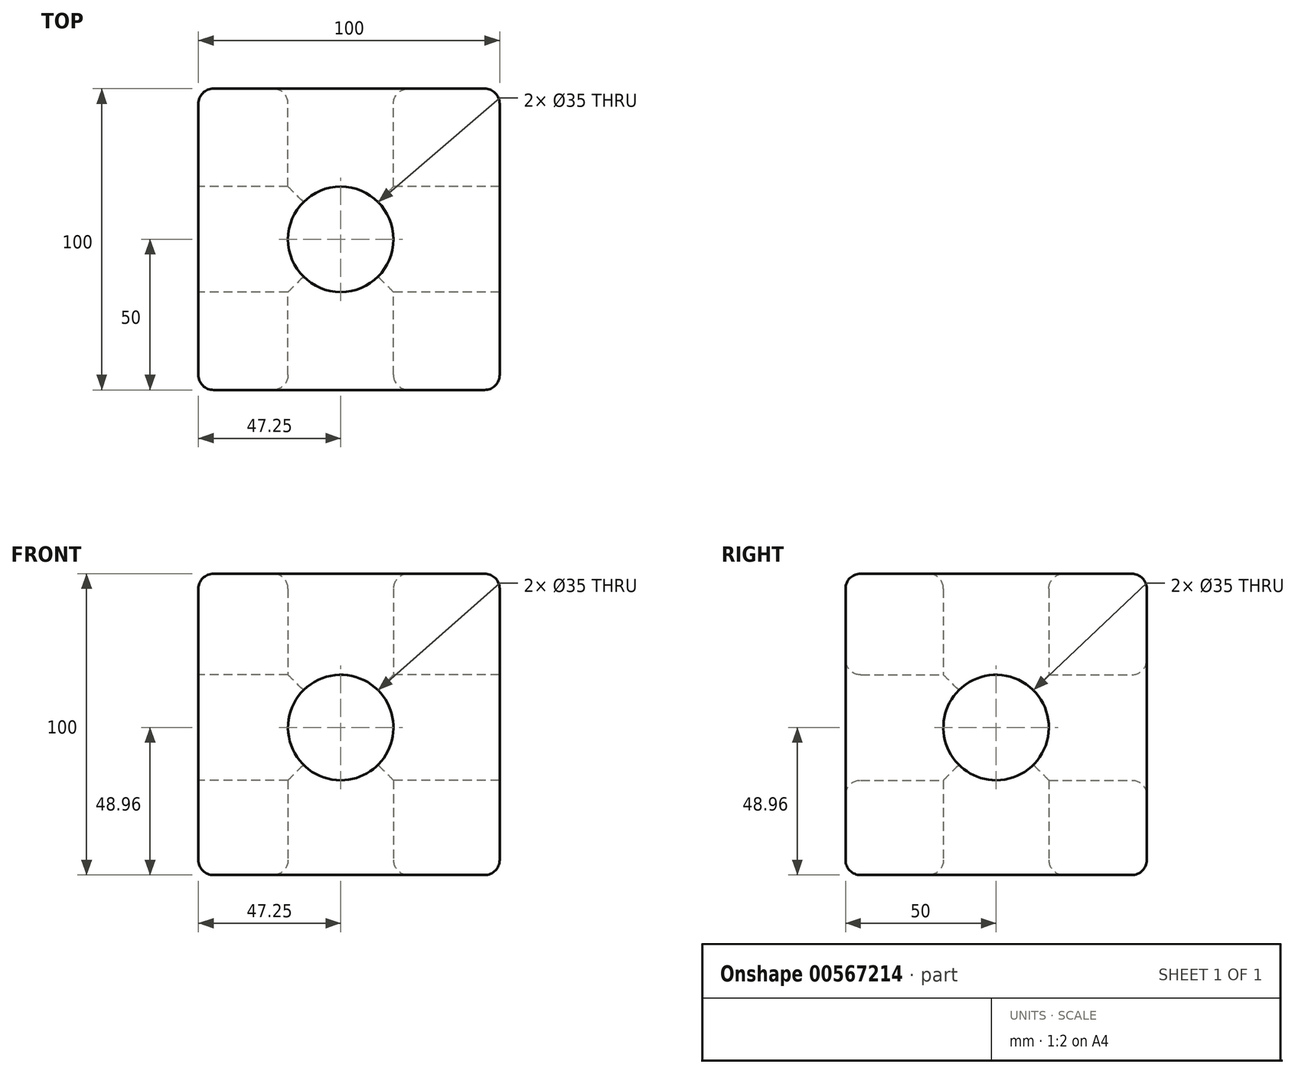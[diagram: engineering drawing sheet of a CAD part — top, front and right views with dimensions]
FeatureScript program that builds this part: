
annotation { "Feature Type Name" : "Feature", "Feature Type Description" : "" }
export const myFeature = defineFeature(function(context is Context, id is Id, definition is map)
    precondition{}
    {
        {
            var Q0;
            Q0=qCreatedBy(makeId("Front.planeOp"),FACE);
            var sketch = newSketch(context, id + "F0", { "sketchPlane" : qUnion([Q0])});
            skLineSegment(sketch, "E0.bottom", {"start": v(-47.25, 51.04) * mm, "end": v(52.75, 51.04) * mm});
            skLineSegment(sketch, "E0.top", {"start": v(-47.25, -48.96) * mm, "end": v(52.75, -48.96) * mm});
            skLineSegment(sketch, "E0.left", {"start": v(-47.25, 51.04) * mm, "end": v(-47.25, -48.96) * mm});
            skLineSegment(sketch, "E0.right", {"start": v(52.75, 51.04) * mm, "end": v(52.75, -48.96) * mm});
            skCircle(sketch, "E1", {"center": v(0, 0) * mm, "radius": 17.5 * mm});
            skSolve(sketch);
        }
        {
            var Q0;
            Q0 = qSketchRegion(id + "F0", true);
            extrude(context, id + "F1", {"entities" : qUnion([Q0]), "endBound" : BoundingType.SYMMETRIC, "depth" : 100 * mm, "offsetDistance" : 25 * mm});
        }
        {
            var Q0;
            Q0=makeQuery(id+"F1.opExtrude","SWEPT_FACE",FACE,{"disambiguationData":[OSD([sQuery(id+"F0.wireOp",EDGE,"E0.left")])]});
            var sketch = newSketch(context, id + "F2", { "sketchPlane" : qUnion([Q0])});
            skCircle(sketch, "E2", {"center": v(0, 0) * mm, "radius": 17.5 * mm});
            skSolve(sketch);
        }
        {
            var Q0;
            Q0 = qSketchRegion(id + "F2", true);
            var Q1;
            Q1=makeQuery(id+"F1.opExtrude","SWEPT_FACE",FACE,{"disambiguationData":[OSD([sQuery(id+"F0.wireOp",EDGE,"E0.right")])]});
            extrude(context, id + "F3", {"entities" : qUnion([Q0]), "operationType" : NewBodyOperationType.REMOVE, "endBound" : BoundingType.UP_TO_SURFACE, "oppositeDirection" : true, "depth" : 25 * mm, "endBoundEntityFace" : qUnion([Q1]), "offsetDistance" : 25 * mm});
        }
        {
            var Q0;
            Q0=makeQuery(id+"F1.opExtrude","SWEPT_FACE",FACE,{"disambiguationData":[OSD([sQuery(id+"F0.wireOp",EDGE,"E0.top")])]});
            var sketch = newSketch(context, id + "F4", { "sketchPlane" : qUnion([Q0])});
            skCircle(sketch, "E3", {"center": v(0, 0) * mm, "radius": 17.5 * mm});
            skSolve(sketch);
        }
        {
            var Q0;
            Q0=makeQuery(id+"F4.imprint","IMPRINT",FACE,{"disambiguationData":[TD([[makeQuery(id+"F4.imprint","IMPRINT",EDGE,{"derivedFrom":sQuery(id+"F4.wireOp",EDGE,"E3")}),1.0]])]});
            var Q1;
            Q1=sQuery(id+"F4.wireOp",EDGE,"E3");
            extrude(context, id + "F5", {"entities" : qUnion([Q0]), "operationType" : NewBodyOperationType.REMOVE, "surfaceEntities" : qUnion([Q1]), "endBound" : BoundingType.SYMMETRIC, "oppositeDirection" : true, "depth" : 202 * mm, "offsetDistance" : 25 * mm});
        }
        {
            var Q0;
            Q0=makeQuery(id+"F1.opExtrude","SWEPT_EDGE",EDGE,{"disambiguationData":[OSD([sQuery(id+"F0.wireOp",EDGE,"E0.bottom"),sQuery(id+"F0.wireOp",EDGE,"E0.right")])]});
            var Q1;
            Q1=makeQuery(id+"F1.opExtrude","CAP_EDGE",EDGE,{"disambiguationData":[OSD([sQuery(id+"F0.wireOp",EDGE,"E0.right")])],"isStart":false});
            var Q2;
            Q2=makeQuery(id+"F1.opExtrude","CAP_EDGE",EDGE,{"disambiguationData":[OSD([sQuery(id+"F0.wireOp",EDGE,"E0.bottom")])],"isStart":false});
            var Q3;
            Q3=makeQuery(id+"F1.opExtrude","SWEPT_EDGE",EDGE,{"disambiguationData":[OSD([sQuery(id+"F0.wireOp",EDGE,"E0.bottom"),sQuery(id+"F0.wireOp",EDGE,"E0.left")])]});
            var Q4;
            Q4=makeQuery(id+"F1.opExtrude","CAP_EDGE",EDGE,{"disambiguationData":[OSD([sQuery(id+"F0.wireOp",EDGE,"E0.bottom")])],"isStart":true});
            var Q5;
            Q5=makeQuery(id+"F1.opExtrude","CAP_EDGE",EDGE,{"disambiguationData":[OSD([sQuery(id+"F0.wireOp",EDGE,"E0.left")])],"isStart":false});
            var Q6;
            Q6=makeQuery(id+"F1.opExtrude","CAP_EDGE",EDGE,{"disambiguationData":[OSD([sQuery(id+"F0.wireOp",EDGE,"E0.top")])],"isStart":false});
            var Q7;
            Q7=makeQuery(id+"F1.opExtrude","SWEPT_EDGE",EDGE,{"disambiguationData":[OSD([sQuery(id+"F0.wireOp",EDGE,"E0.top"),sQuery(id+"F0.wireOp",EDGE,"E0.right")])]});
            var Q8;
            Q8=makeQuery(id+"F1.opExtrude","CAP_EDGE",EDGE,{"disambiguationData":[OSD([sQuery(id+"F0.wireOp",EDGE,"E0.right")])],"isStart":true});
            var Q9;
            Q9=makeQuery(id+"F1.opExtrude","CAP_EDGE",EDGE,{"disambiguationData":[OSD([sQuery(id+"F0.wireOp",EDGE,"E0.left")])],"isStart":true});
            var Q10;
            Q10=makeQuery(id+"F1.opExtrude","CAP_EDGE",EDGE,{"disambiguationData":[OSD([sQuery(id+"F0.wireOp",EDGE,"E0.top")])],"isStart":true});
            var Q11;
            Q11=makeQuery(id+"F1.opExtrude","SWEPT_EDGE",EDGE,{"disambiguationData":[OSD([sQuery(id+"F0.wireOp",EDGE,"E0.top"),sQuery(id+"F0.wireOp",EDGE,"E0.left")])]});
            var Q12;
            Q12=makeQuery(id+"F1.opExtrude","CAP_EDGE",EDGE,{"disambiguationData":[OSD([sQuery(id+"F0.wireOp",EDGE,"E1")])],"isStart":true});
            var Q13;
            Q13=makeQuery(id+"F3.boolean.opBoolean","COPY",EDGE,{"derivedFrom":makeQuery(id+"F3.opExtrude","CAP_EDGE",EDGE,{"disambiguationData":[OSD([sQuery(id+"F2.wireOp",EDGE,"E2")])],"isStart":false})});
            var Q14;
            Q14=makeQuery(id+"F5.boolean.opBoolean","INTERSECT",EDGE,{"derivedFrom":[makeQuery(id+"F1.opExtrude","SWEPT_FACE",FACE,{"disambiguationData":[OSD([sQuery(id+"F0.wireOp",EDGE,"E0.bottom")])]}),makeQuery(id+"F5.opExtrude","SWEPT_FACE",FACE,{"disambiguationData":[OSD([sQuery(id+"F4.wireOp",EDGE,"E3")])]})]});
            var Q15;
            Q15=makeQuery(id+"F5.boolean.opBoolean","INTERSECT",EDGE,{"derivedFrom":[makeQuery(id+"F1.opExtrude","SWEPT_FACE",FACE,{"disambiguationData":[OSD([sQuery(id+"F0.wireOp",EDGE,"E0.top")])]}),makeQuery(id+"F5.opExtrude","SWEPT_FACE",FACE,{"disambiguationData":[OSD([sQuery(id+"F4.wireOp",EDGE,"E3")])]})]});
            var Q16;
            Q16=makeQuery(id+"F3.boolean.opBoolean","COPY",EDGE,{"derivedFrom":makeQuery(id+"F3.opExtrude","CAP_EDGE",EDGE,{"disambiguationData":[OSD([sQuery(id+"F2.wireOp",EDGE,"E2")])],"isStart":true})});
            var Q17;
            Q17=makeQuery(id+"F1.opExtrude","CAP_EDGE",EDGE,{"disambiguationData":[OSD([sQuery(id+"F0.wireOp",EDGE,"E1")])],"isStart":false});
            fillet(context, id + "F6", {"entities" : qUnion([Q0, Q1, Q2, Q3, Q4, Q5, Q6, Q7, Q8, Q9, Q10, Q11, Q12, Q13, Q14, Q15, Q16, Q17]), "radius" : 5 * mm, "tangentPropagation" : true, "allowEdgeOverflow" : false});
        }
    });
